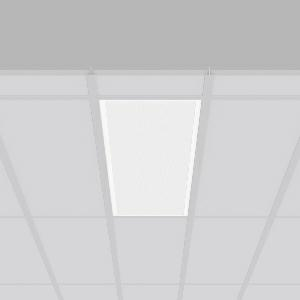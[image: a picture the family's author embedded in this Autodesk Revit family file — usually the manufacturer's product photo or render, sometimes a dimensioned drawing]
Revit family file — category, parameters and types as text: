
# Revit family: sidelite_eco_312366_002_1_790_8180
name_source: partatom
category: Lighting Fixtures
units: mm (PartAtom-declared; Revit-internal decimal feet)

## family parameters
Cut with Voids When Loaded = No
Host = Face
Light Source = No
Part Type = Normal
Room Calculation Point = No
Round Connector Dimension = Use Diameter
Shared = No

## types (1)
- MultiLumen 1 (1 x LED Modul 840, 3500 lm, 4000)
    Apparent Load = 29 VA
    CIE Flux Codes = 63 88 97 100 100
    Color Rendering = 80
    Color Temperature = 4000
    Default Elevation = 1800 mm
    Description = Series: SIDELITE ECO
Highly economical recessed luminaire with progressive LED technology. Frame made of aluminium, powder-coated. Diffuser plastic microprismatic. Lightguide and diffuser made of non-yellowing plastic (PMMA). Lateral light emission (RZB SIDELITE technology) for homogeneous light distribution. External driver. External driver with simple plug-in locking system and extended converter connecting cable to luminaire (1.90 m). MultiLumen: 4 steps adjustable luminous flux. Factory setting is the lowest offered step. Luminaire can be used with accessories (to be ordered separately) for recessed, surface mounting or as pendant luminaire. Perfect for office areas (RUG < 19) and environments with computer screens in accordance with EN 12464-1. Qualified for use in the food and drink industry. 
Colour: white
Length: 1195 mm
Width: 295 mm
Cut-out length: 1180 mm
Cut-out width: 280 mm
Recess height: 160 mm
Luminaire: recess height: 37 mm
Lamp: LED
Socket: without socket
Colour temperature: 4000K
Colour rendering index (CRI): 80
System power: 29 W
Rated luminous flux: 3500 lm
Luminous efficiency: 121 lm/W
System power 2: 33 W
Rated luminous flux 2: 3850 lm
Luminous efficiency 2: 117 lm/W
System power 3: 35 W
Rated luminous flux 3: 4050 lm
Luminous efficiency 3: 116 lm/W
System power 4: 38 W
Rated luminous flux 4: 4400 lm
Luminous efficiency 4: 116 lm/W
Control gear: Regulated power supply
Protection class: II
Type of protection: IP 40
    Height = 0 mm  [stored 0 ft]
    Lamp = 1 x LED Modul 840
    Lamp Light Flux = 3500 lm
    Lamp count = 1
    Length = 1195 mm
    Lifetime = 50000 h
    Luminous efficacy = 121 lm/W
    Manufacturer = RZB
    ModVariant = No
    Model = 312366.002.1.790
    Mounting Place = Ceiling
    Mounting Type = Recessed
    Number of Poles = 1
    OnlyDefault = Yes
    Power Factor = 1
    Product Name = SIDELITE ECO
    Product group = Recessed modular luminaires
    ProductGroupID = 406
    Protection Class = Protection class II
    Protection Degree = IP 20
    RLX_Detail_Level = 1
    RLX_Emergency_Light_Flux = 0 lm
    RLX_Emergency_Type = 0
    RLX_Emergency_Type_DB = No
    RlxData = <blob elided: 36005 chars, md5=1fd5b7e3>
    Socket = socket
    Standby Power = 0 W
    System Light Flux = 3500 lm
    System Power = 29 W
    Type Comments = MultiLumen 1
    Type Image = 312366.002.jpg
    URL = http://relux.com
    VarID = multilumen_1
    Voltage = 230 V
    Voltage Range = 220-240 V
    Weight = 0.00 kg
    Width = 295 mm

note: [stored X ft] marks values corroborated as IEEE doubles in the binary element streams (Revit-internal decimal feet)

## geometry (parser evidence)
native form markers: Blend x4, Sweep x11
no freeform markers — native parametric forms only
